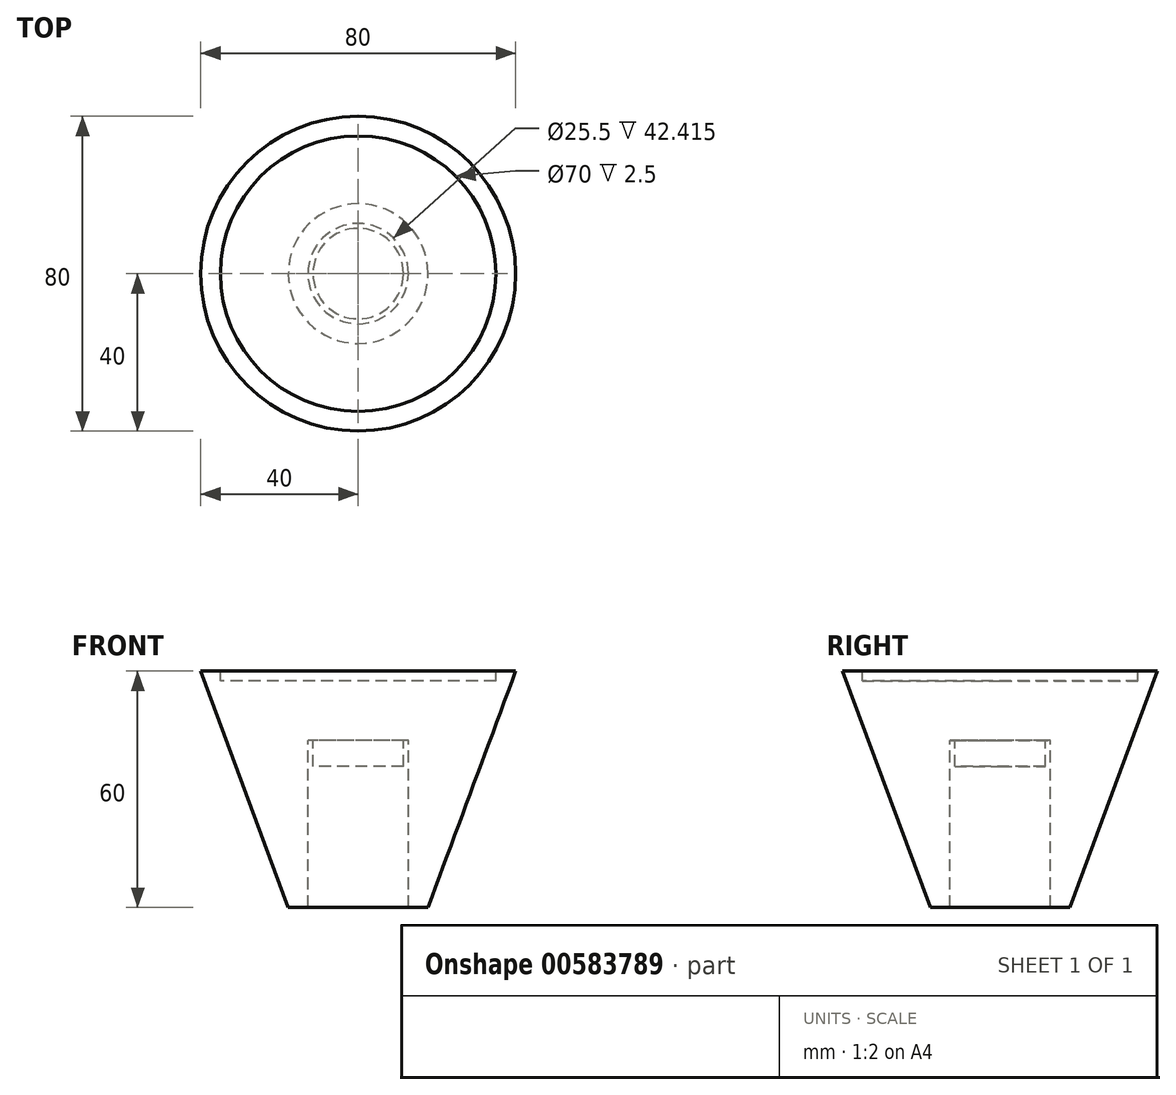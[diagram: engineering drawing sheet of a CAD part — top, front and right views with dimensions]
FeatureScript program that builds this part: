
annotation { "Feature Type Name" : "Feature", "Feature Type Description" : "" }
export const myFeature = defineFeature(function(context is Context, id is Id, definition is map)
    precondition{}
    {
        {
            var Q0;
            Q0=qCreatedBy(makeId("Front.planeOp"),FACE);
            var sketch = newSketch(context, id + "F0", { "sketchPlane" : qUnion([Q0])});
            skLineSegment(sketch, "E0.MirrorCS", {"start": v(-17.75, -60) * mm, "end": v(-40, 0) * mm});
            skLineSegment(sketch, "E1.MirrorCS", {"start": v(-12.75, -60) * mm, "end": v(-17.75, -60) * mm});
            skLineSegment(sketch, "E2.MirrorCS", {"start": v(-12.75, -17.59) * mm, "end": v(-12.75, -60) * mm});
            skLineSegment(sketch, "E3.MirrorCS", {"start": v(-11.5, -24.23) * mm, "end": v(-11.5, -17.59) * mm});
            skLineSegment(sketch, "E4.MirrorCS", {"start": v(-11.5, -17.59) * mm, "end": v(-12.75, -17.59) * mm});
            skLineSegment(sketch, "E5.MirrorCS", {"start": v(0, -24.23) * mm, "end": v(-11.5, -24.23) * mm});
            skLineSegment(sketch, "E6.MirrorCS", {"start": v(0, -2.5) * mm, "end": v(0, -24.23) * mm});
            skLineSegment(sketch, "E7", {"start": v(-35, 0) * mm, "end": v(-35, -2.5) * mm});
            skLineSegment(sketch, "E8", {"start": v(-35, -2.5) * mm, "end": v(0, -2.5) * mm});
            skLineSegment(sketch, "E9", {"start": v(-40, 0) * mm, "end": v(-35, 0) * mm});
            skSolve(sketch);
        }
        {
            var Q0;
            Q0=makeQuery(id+"F0.imprint","IMPRINT",FACE,{"disambiguationData":[TD([[makeQuery(id+"F0.imprint","IMPRINT",EDGE,{"derivedFrom":sQuery(id+"F0.wireOp",EDGE,"E0.MirrorCS")}),-1.0]])]});
            var Q1;
            Q1=sQuery(id+"F0.wireOp",EDGE,"E6.MirrorCS");
            revolve(context, id + "F1", {"entities" : qUnion([Q0]), "axis" : qUnion([Q1]), "revolveType" : RevolveType.FULL});
        }
    });
